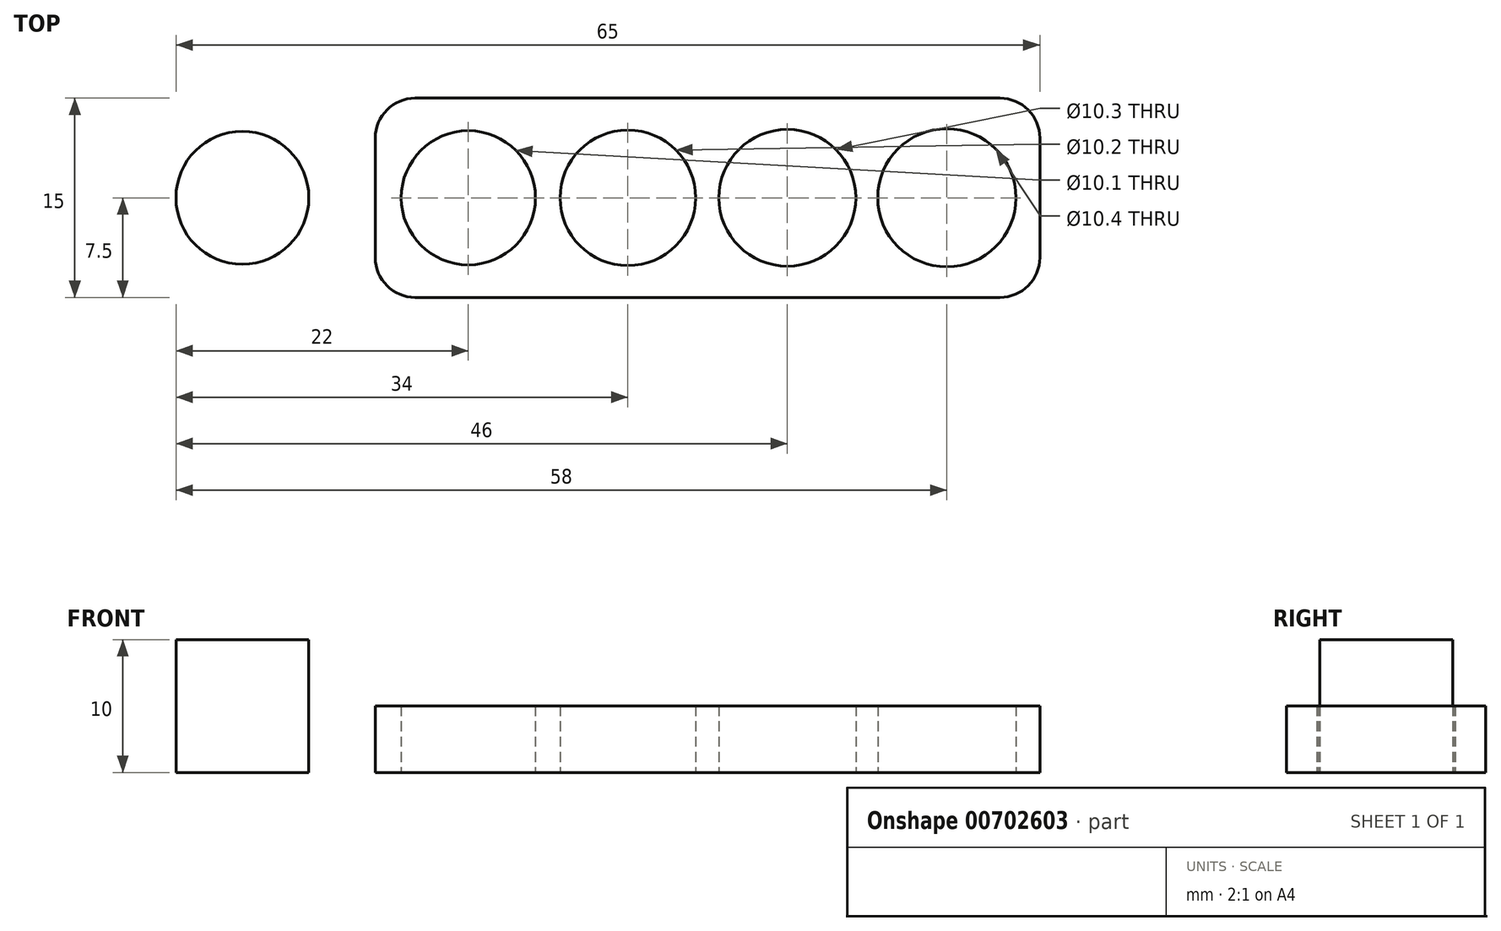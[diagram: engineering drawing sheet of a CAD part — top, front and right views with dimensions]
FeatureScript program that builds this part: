
annotation { "Feature Type Name" : "Feature", "Feature Type Description" : "" }
export const myFeature = defineFeature(function(context is Context, id is Id, definition is map)
    precondition{}
    {
        {
            var Q0;
            Q0=qCreatedBy(makeId("Top.planeOp"),FACE);
            var sketch = newSketch(context, id + "F0", { "sketchPlane" : qUnion([Q0])});
            skCircle(sketch, "E0", {"center": v(0, 0) * mm, "radius": 5 * mm});
            skCircle(sketch, "E1", {"center": v(17, 0) * mm, "radius": 5.05 * mm});
            skCircle(sketch, "E2", {"center": v(29, 0) * mm, "radius": 5.1 * mm});
            skCircle(sketch, "E3", {"center": v(41, 0) * mm, "radius": 5.15 * mm});
            skCircle(sketch, "E4", {"center": v(53, 0) * mm, "radius": 5.2 * mm});
            skLineSegment(sketch, "E5.bottom", {"start": v(10, -7.5) * mm, "end": v(60, -7.5) * mm});
            skLineSegment(sketch, "E5.top", {"start": v(10, 7.5) * mm, "end": v(60, 7.5) * mm});
            skLineSegment(sketch, "E5.left", {"start": v(10, -7.5) * mm, "end": v(10, 7.5) * mm});
            skLineSegment(sketch, "E5.right", {"start": v(60, -7.5) * mm, "end": v(60, 7.5) * mm});
            skLineSegment(sketch, "E6", {"start": v(10, 0) * mm, "end": v(60, 0) * mm, "construction": true});
            skSolve(sketch);
        }
        {
            var Q0;
            Q0=makeQuery(id+"F0.imprint","IMPRINT",FACE,{"disambiguationData":[TD([[makeQuery(id+"F0.imprint","IMPRINT",EDGE,{"derivedFrom":sQuery(id+"F0.wireOp",EDGE,"E1")}),-1.0]])]});
            extrude(context, id + "F1", {"entities" : qUnion([Q0]), "depth" : 5 * mm, "offsetDistance" : 25 * mm});
        }
        {
            var Q0;
            Q0=makeQuery(id+"F0.imprint","IMPRINT",FACE,{"disambiguationData":[TD([[makeQuery(id+"F0.imprint","IMPRINT",EDGE,{"derivedFrom":sQuery(id+"F0.wireOp",EDGE,"E0")}),1.0]])]});
            extrude(context, id + "F2", {"entities" : qUnion([Q0]), "depth" : 10 * mm, "offsetDistance" : 25 * mm});
        }
        {
            var Q0;
            Q0=makeQuery(id+"F1.opExtrude","SWEPT_EDGE",EDGE,{"disambiguationData":[OSD([sQuery(id+"F0.wireOp",EDGE,"E5.bottom"),sQuery(id+"F0.wireOp",EDGE,"E5.left")])]});
            var Q1;
            Q1=makeQuery(id+"F1.opExtrude","SWEPT_EDGE",EDGE,{"disambiguationData":[OSD([sQuery(id+"F0.wireOp",EDGE,"E5.bottom"),sQuery(id+"F0.wireOp",EDGE,"E5.right")])]});
            var Q2;
            Q2=makeQuery(id+"F1.opExtrude","SWEPT_EDGE",EDGE,{"disambiguationData":[OSD([sQuery(id+"F0.wireOp",EDGE,"E5.top"),sQuery(id+"F0.wireOp",EDGE,"E5.right")])]});
            var Q3;
            Q3=makeQuery(id+"F1.opExtrude","SWEPT_EDGE",EDGE,{"disambiguationData":[OSD([sQuery(id+"F0.wireOp",EDGE,"E5.top"),sQuery(id+"F0.wireOp",EDGE,"E5.left")])]});
            fillet(context, id + "F3", {"entities" : qUnion([Q0, Q1, Q2, Q3]), "radius" : 3 * mm, "tangentPropagation" : true, "allowEdgeOverflow" : false});
        }
    });
